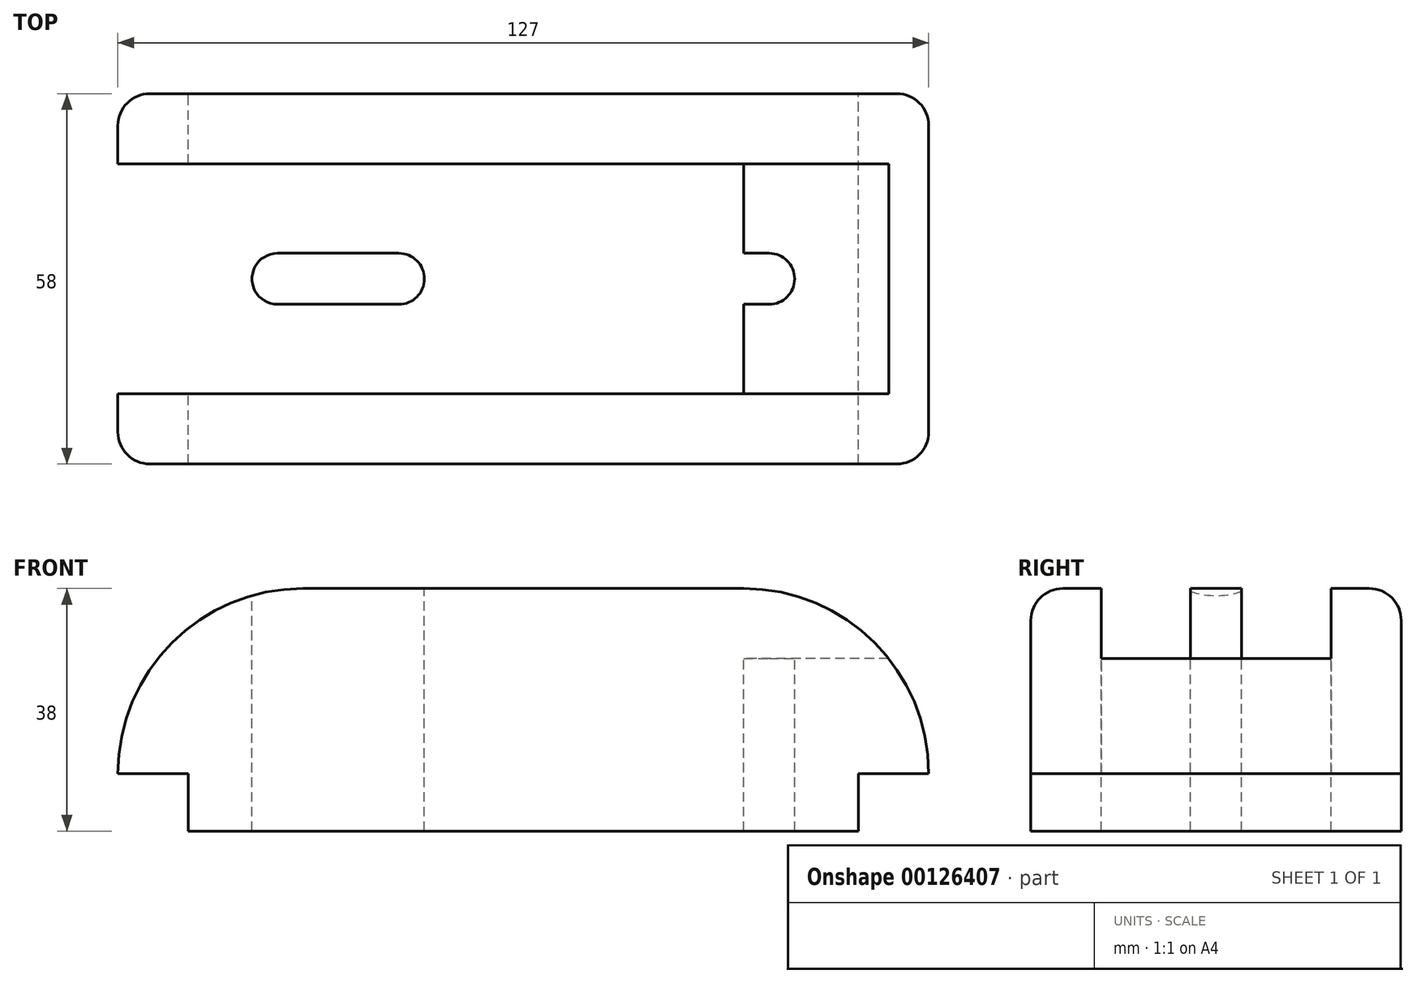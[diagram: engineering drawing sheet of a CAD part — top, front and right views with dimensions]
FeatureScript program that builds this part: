
annotation { "Feature Type Name" : "Feature", "Feature Type Description" : "" }
export const myFeature = defineFeature(function(context is Context, id is Id, definition is map)
    precondition{}
    {
        {
            var Q0;
            Q0=qCreatedBy(makeId("Front.planeOp"),FACE);
            var sketch = newSketch(context, id + "F0", { "sketchPlane" : qUnion([Q0])});
            skLineSegment(sketch, "E0", {"start": v(0, 0) * mm, "end": v(52.5, 0) * mm});
            skLineSegment(sketch, "E1", {"start": v(52.5, 0) * mm, "end": v(52.5, 9) * mm});
            skLineSegment(sketch, "E2", {"start": v(52.5, 9) * mm, "end": v(63.5, 9) * mm});
            skLineSegment(sketch, "E3", {"start": v(0, 38) * mm, "end": v(34.5, 38) * mm});
            skArc(sketch, "E4", {"start": v(63.5, 9) * mm, "mid": v(55, 29.5) * mm, "end": v(34.5, 38) * mm});
            skLineSegment(sketch, "E5.MirrorCS", {"start": v(0, 38) * mm, "end": v(-34.5, 38) * mm});
            skArc(sketch, "E6.MirrorCS", {"start": v(-63.5, 9) * mm, "mid": v(-55, 29.5) * mm, "end": v(-34.5, 38) * mm});
            skLineSegment(sketch, "E7.MirrorCS", {"start": v(-52.5, 9) * mm, "end": v(-63.5, 9) * mm});
            skLineSegment(sketch, "E8.MirrorCS", {"start": v(0, 0) * mm, "end": v(-52.5, 0) * mm});
            skLineSegment(sketch, "E9.MirrorCS", {"start": v(-52.5, 0) * mm, "end": v(-52.5, 9) * mm});
            skSolve(sketch);
        }
        {
            var Q0;
            Q0=qSketchRegion(id+"F0",true);
            extrude(context, id + "F1", {"entities" : qUnion([Q0]), "endBound" : BoundingType.SYMMETRIC, "depth" : 58 * mm});
        }
        {
            var Q0;
            Q0=makeQuery(id+"F1.opExtrude","SWEPT_FACE",FACE,{"disambiguationData":[OSD([sQuery(id+"F0.wireOp",EDGE,"E3"),sQuery(id+"F0.wireOp",EDGE,"E5.MirrorCS")])]});
            var sketch = newSketch(context, id + "F2", { "sketchPlane" : qUnion([Q0])});
            skLineSegment(sketch, "E10.bottom", {"start": v(-34.5, 18) * mm, "end": v(34.5, 18) * mm});
            skLineSegment(sketch, "E10.top", {"start": v(-34.5, -18) * mm, "end": v(34.5, -18) * mm});
            skLineSegment(sketch, "E10.left", {"start": v(-34.5, 18) * mm, "end": v(-34.5, -18) * mm});
            skLineSegment(sketch, "E10.right", {"start": v(34.5, 18) * mm, "end": v(34.5, -18) * mm});
            skLineSegment(sketch, "E11.bottom", {"start": v(34.5, 18) * mm, "end": v(74.5, 18) * mm});
            skLineSegment(sketch, "E11.top", {"start": v(34.5, -18) * mm, "end": v(74.5, -18) * mm});
            skLineSegment(sketch, "E11.right", {"start": v(74.5, 18) * mm, "end": v(74.5, -18) * mm});
            skLineSegment(sketch, "E12.bottom", {"start": v(-34.5, 18) * mm, "end": v(-67.5, 18) * mm});
            skLineSegment(sketch, "E12.top", {"start": v(-34.5, -18) * mm, "end": v(-67.5, -18) * mm});
            skLineSegment(sketch, "E12.right", {"start": v(-67.5, 18) * mm, "end": v(-67.5, -18) * mm});
            skPoint(sketch, "E13", {"position": v(-34.5, 0) * mm});
            skLineSegment(sketch, "E14", {"start": v(-34.5, 0) * mm, "end": v(-34.5, 0) * mm});
            skLineSegment(sketch, "E15", {"start": v(19.5, -4) * mm, "end": v(38.5, -4) * mm});
            skLineSegment(sketch, "E16", {"start": v(19.5, 4) * mm, "end": v(38.5, 4) * mm});
            skArc(sketch, "E17", {"start": v(19.5, 4) * mm, "mid": v(15.5, 0) * mm, "end": v(19.5, -4) * mm});
            skArc(sketch, "E18", {"start": v(38.5, -4) * mm, "mid": v(42.5, 0) * mm, "end": v(38.5, 4) * mm});
            skLineSegment(sketch, "E19", {"start": v(29, -4) * mm, "end": v(29, -29) * mm, "construction": true});
            skLineSegment(sketch, "E20", {"start": v(29, 4) * mm, "end": v(29, 29) * mm, "construction": true});
            skArc(sketch, "E21.MirrorCS", {"start": v(-19.5, 4) * mm, "mid": v(-15.5, 0) * mm, "end": v(-19.5, -4) * mm});
            skLineSegment(sketch, "E22.MirrorCS", {"start": v(-19.5, -4) * mm, "end": v(-38.5, -4) * mm});
            skLineSegment(sketch, "E23.MirrorCS", {"start": v(-19.5, 4) * mm, "end": v(-38.5, 4) * mm});
            skArc(sketch, "E24.MirrorCS", {"start": v(-38.5, -4) * mm, "mid": v(-42.5, 0) * mm, "end": v(-38.5, 4) * mm});
            skSolve(sketch);
        }
        {
            var Q0;
            {var subQ5=sQuery(id+"F2.wireOp",EDGE,"E21.MirrorCS");Q0=makeQuery(id+"F2.imprint","IMPRINT",FACE,{"disambiguationData":[TD([[makeQuery(id+"F2.imprint","IMPRINT",EDGE,{"derivedFrom":subQ5}),-1.0]])]});}
            var Q1;
            {var subQ5=sQuery(id+"F2.wireOp",EDGE,"E24.MirrorCS");Q1=makeQuery(id+"F2.imprint","IMPRINT",FACE,{"disambiguationData":[TD([[makeQuery(id+"F2.imprint","IMPRINT",EDGE,{"derivedFrom":subQ5}),-1.0]])]});}
            var Q2;
            {var subQ5=sQuery(id+"F2.wireOp",EDGE,"E17");Q2=makeQuery(id+"F2.imprint","IMPRINT",FACE,{"disambiguationData":[TD([[makeQuery(id+"F2.imprint","IMPRINT",EDGE,{"derivedFrom":subQ5}),1.0]])]});}
            var Q3;
            {var subQ5=sQuery(id+"F2.wireOp",EDGE,"E18");Q3=makeQuery(id+"F2.imprint","IMPRINT",FACE,{"disambiguationData":[TD([[makeQuery(id+"F2.imprint","IMPRINT",EDGE,{"derivedFrom":subQ5}),1.0]])]});}
            extrude(context, id + "F3", {"entities" : qUnion([Q0, Q1, Q2, Q3]), "operationType" : NewBodyOperationType.REMOVE, "endBound" : BoundingType.THROUGH_ALL, "oppositeDirection" : true, "depth" : 25 * mm});
        }
        {
            var Q0;
            {var subQ1=sQuery(id+"F2.wireOp",EDGE,"E12.bottom");Q0=makeQuery(id+"F2.imprint","IMPRINT",FACE,{"disambiguationData":[TD([[makeQuery(id+"F2.imprint","IMPRINT",EDGE,{"derivedFrom":subQ1}),1.0]])]});}
            var Q1;
            {var subQ1=sQuery(id+"F2.wireOp",EDGE,"E10.bottom");Q1=makeQuery(id+"F2.imprint","IMPRINT",FACE,{"disambiguationData":[TD([[makeQuery(id+"F2.imprint","IMPRINT",EDGE,{"derivedFrom":subQ1}),-1.0]])]});}
            var Q2;
            {var subQ1=sQuery(id+"F2.wireOp",EDGE,"E11.bottom");Q2=makeQuery(id+"F2.imprint","IMPRINT",FACE,{"disambiguationData":[TD([[makeQuery(id+"F2.imprint","IMPRINT",EDGE,{"derivedFrom":subQ1}),-1.0]])]});}
            extrude(context, id + "F4", {"entities" : qUnion([Q0, Q1, Q2]), "operationType" : NewBodyOperationType.REMOVE, "oppositeDirection" : true, "depth" : 11 * mm});
        }
        {
            var Q0;
            Q0=makeQuery(id+"F1.opExtrude","CAP_EDGE",EDGE,{"disambiguationData":[OSD([sQuery(id+"F0.wireOp",EDGE,"E3"),sQuery(id+"F0.wireOp",EDGE,"E5.MirrorCS")])],"isStart":false});
            var Q1;
            Q1=makeQuery(id+"F1.opExtrude","CAP_EDGE",EDGE,{"disambiguationData":[OSD([sQuery(id+"F0.wireOp",EDGE,"E3"),sQuery(id+"F0.wireOp",EDGE,"E5.MirrorCS")])],"isStart":true});
            fillet(context, id + "F5", {"entities" : qUnion([Q0, Q1]), "radius" : 5 * mm, "tangentPropagation" : true, "allowEdgeOverflow" : false});
        }
    });
